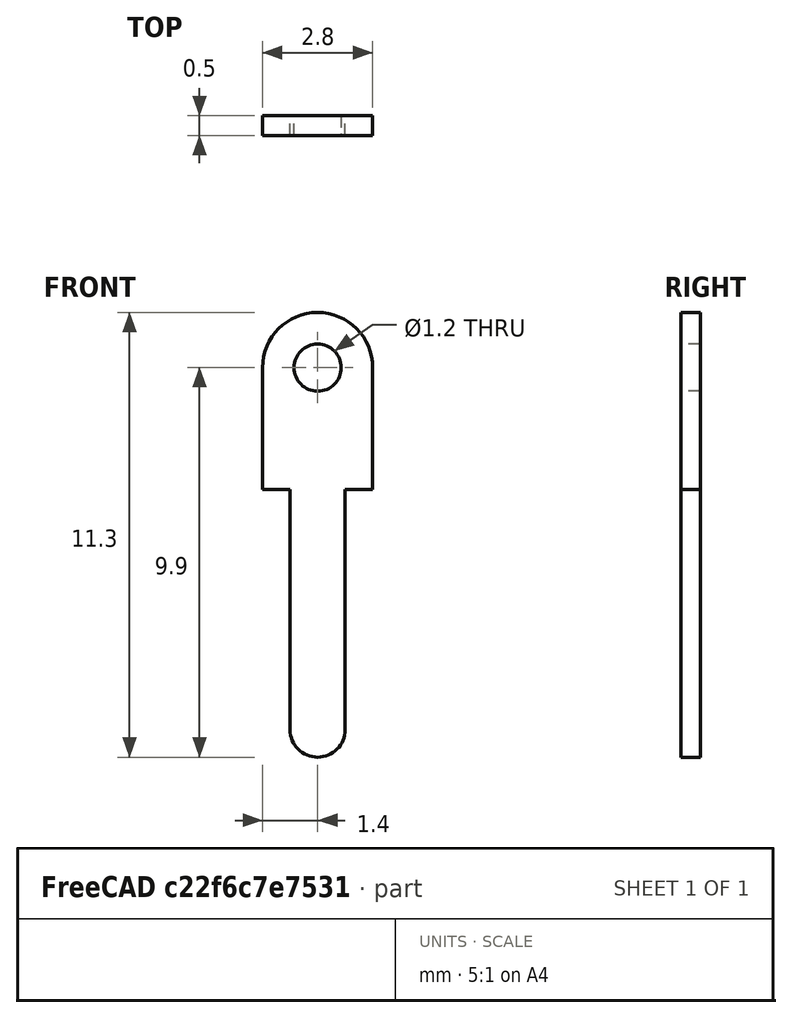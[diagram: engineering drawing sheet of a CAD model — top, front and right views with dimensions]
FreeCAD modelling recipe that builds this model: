
FCSTD DOCUMENT  (FreeCAD 0.17R12018 (Git))
Label: Pin_d1.3mm_L11.3mm_W2.8mm_Flat
License: All rights reserved
LicenseURL: http://en.wikipedia.org/wiki/All_rights_reserved
objects: Spreadsheet::Sheet×1, Sketcher::SketchObject×1, PartDesign::Pad×1, PartDesign::Body×1, App::Part×1
note: 4 computed .brp shape members not serialized (recipe doc carries the construction recipe); baked Part::Feature solids carry a one-line shape summary decoded from their .brp

FEATURE [Spreadsheet::Sheet] Spreadsheet  label="dimensions"
  cells = A1="L"; B1(L)=11.300000000000001; A2="Wtop"; B2(Wtop)=2.7999999999999998; A3="Wbottom"; B3(Wbottom)=1.3999999999999999; A4="Lbottom"; B4(Lbottom)=6.7999999999999998; A5="Wfork"; B5(Wfork)=1.2; A7="thick"; B7(thick)=0.5
FEATURE [Sketcher::SketchObject] Sketch
  MapMode = 5
  Placement = pos=(0,0,0) rot=(0,0.707107,0.707107;3.14159rad)
  Support = -> [XZ_Plane001]
  expr: Constraints[19] = dimensions.Lbottom - dimensions.Wbottom / 2
  expr: Constraints[21] = (dimensions.Wtop - dimensions.Wbottom) / 2
  expr: Constraints[20] = dimensions.Wbottom
  expr: Constraints[14] = dimensions.L - dimensions.Lbottom - dimensions.Wtop / 2
  expr: Constraints[22] = dimensions.Wtop
  expr: Constraints[25] = dimensions.Wfork / 2
  sketch-geometry (11):
    g0: LineSegment StartX=-1.4 StartY=3.1 StartZ=0 EndX=-1.4 EndY=0 EndZ=0
    g1: LineSegment StartX=-1.4 StartY=0 StartZ=0 EndX=-0.7 EndY=0 EndZ=0
    g2: LineSegment StartX=-0.7 StartY=0 StartZ=0 EndX=-0.7 EndY=-6.1 EndZ=0
    g3: LineSegment StartX=0.7 StartY=0 StartZ=0 EndX=0.7 EndY=-6.1 EndZ=0
    g4: LineSegment StartX=0.7 StartY=0 StartZ=0 EndX=1.4 EndY=0 EndZ=0
    g5: LineSegment StartX=1.4 StartY=0 StartZ=0 EndX=1.4 EndY=3.1 EndZ=0
    g6: ArcOfCircle CenterX=0 CenterY=-6.1 CenterZ=0 NormalX=0 NormalY=0 NormalZ=1 Radius=0.7 StartAngle=3.14159 EndAngle=6.28319
    g7: LineSegment [constr] StartX=-0.7 StartY=-6.1 StartZ=0 EndX=0.7 EndY=-6.1 EndZ=0
    g8: Circle CenterX=0 CenterY=3.1 CenterZ=0 NormalX=0 NormalY=0 NormalZ=1 Radius=0.6
    g9: ArcOfCircle CenterX=0 CenterY=3.1 CenterZ=0 NormalX=0 NormalY=0 NormalZ=1 Radius=1.4 StartAngle=0 EndAngle=3.14159
    g10: LineSegment [constr] StartX=-1.4 StartY=3.1 StartZ=0 EndX=1.4 EndY=3.1 EndZ=0
  constraints (34):
    c: PointOnObject(g3,g-1)
    c: PointOnObject(g6,g-2)
    c: Coincident(g7,g3)
    c: Coincident(g7,g2)
    c: Coincident(g2,g6)
    c: Coincident(g3,g6)
    c: PointOnObject(g6,g7)
    c: Horizontal(g7)
    c: Vertical(g3)
    c: Vertical(g2)
    c: Horizontal(g1)
    c: Horizontal(g4)
    c: Vertical(g5)
    c: Vertical(g0)
    c: DistanceY(g5,g5) = 3.1
    c: Coincident(g5,g4)
    c: Coincident(g0,g1)
    c: Coincident(g4,g3)
    c: Coincident(g1,g2)
    c: DistanceY(g3,g3) = 6.1
    c: DistanceX(g2,g3) = 1.4
    c: DistanceX(g1,g1) = 0.7
    c: DistanceX(g0,g5) = 2.8
    c: PointOnObject(g1,g-1)
    c: PointOnObject(g8,g-2)
    c: Radius(g8) = 0.6
    c: PointOnObject(g9,g-2)
    c: Coincident(g9,g0)
    c: Coincident(g9,g5)
    c: Coincident(g10,g0)
    c: Coincident(g10,g5)
    c: Horizontal(g10)
    c: PointOnObject(g9,g10)
    c: PointOnObject(g8,g10)
FEATURE [PartDesign::Pad] Pad  label="Pin_d1.3mm_L11.3mm_W2.8mm_Flat"
  Length = 0.5
  Length2 = 100
  Midplane = true
  Placement = pos=(0,0,0) rot=(1,0,0;1.5708rad)
  Profile = -> Sketch
  Type = 0
  expr: Length = dimensions.thick
FEATURE [PartDesign::Body] PadBody  label="Body"
  Group = -> [Sketch,Pad]
  Origin = -> Origin001
  Tip = -> Pad
FEATURE [App::Part] Part
  Group = -> [PadBody]
  License = CC BY 3.0
  LicenseURL = http://creativecommons.org/licenses/by/3.0/
  Origin = -> Origin
